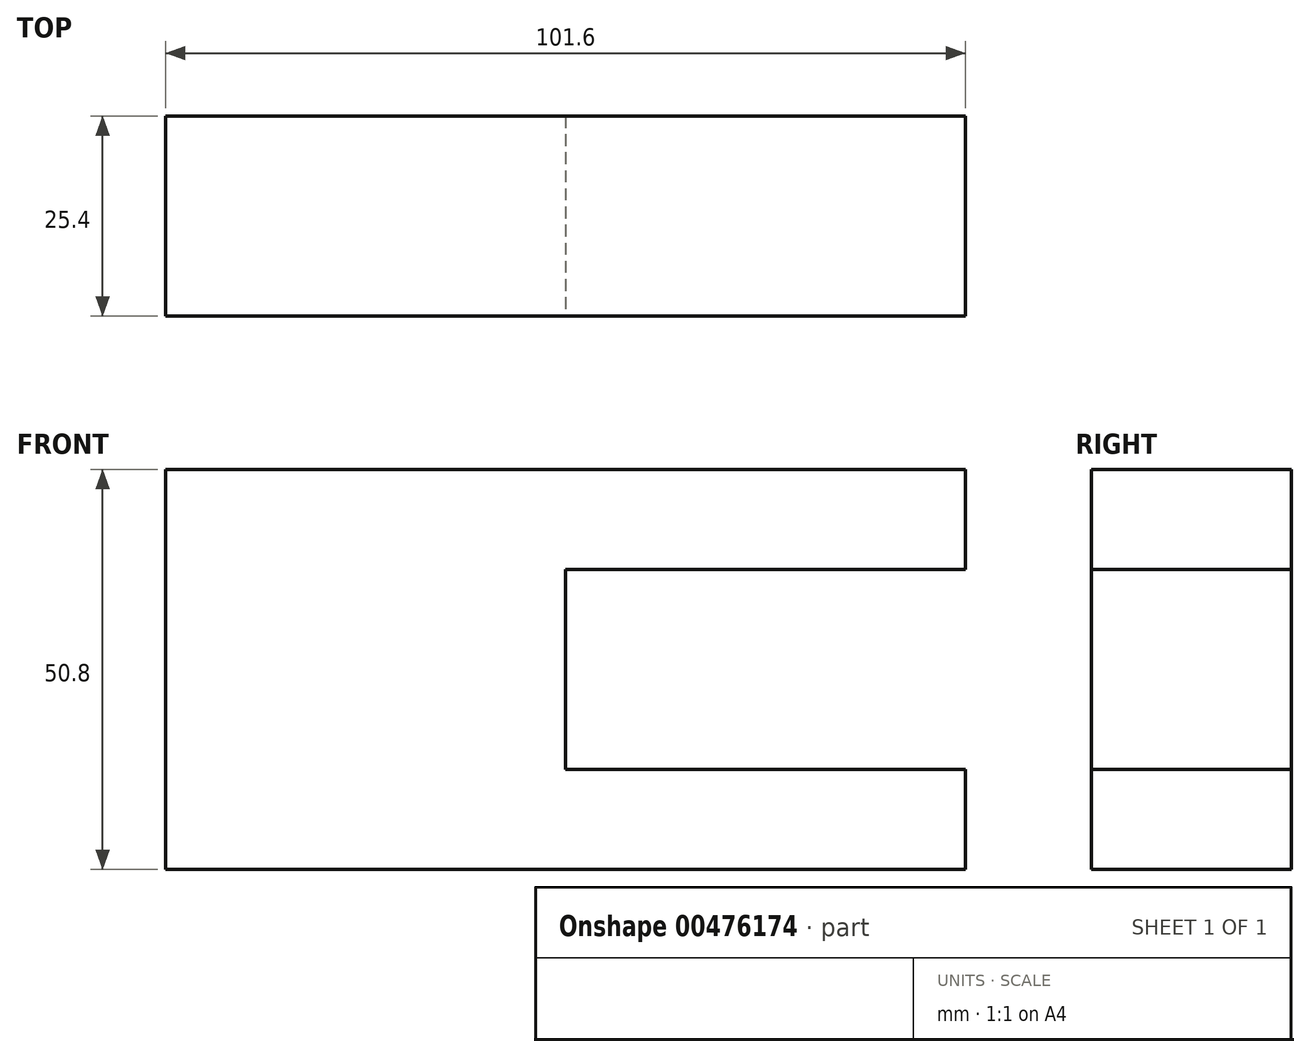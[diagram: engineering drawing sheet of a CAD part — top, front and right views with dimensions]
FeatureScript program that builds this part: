
annotation { "Feature Type Name" : "Feature", "Feature Type Description" : "" }
export const myFeature = defineFeature(function(context is Context, id is Id, definition is map)
    precondition{}
    {
        {
            var Q0;
            Q0=qCreatedBy(makeId("Front.planeOp"),FACE);
            var sketch = newSketch(context, id + "F0", { "sketchPlane" : qUnion([Q0])});
            skLineSegment(sketch, "E0.bottom", {"start": v(50.8, -25.4) * mm, "end": v(-50.8, -25.4) * mm});
            skLineSegment(sketch, "E0.top", {"start": v(50.8, 25.4) * mm, "end": v(-50.8, 25.4) * mm});
            skLineSegment(sketch, "E0.left", {"start": v(50.8, -25.4) * mm, "end": v(50.8, 25.4) * mm});
            skLineSegment(sketch, "E0.right", {"start": v(-50.8, -25.4) * mm, "end": v(-50.8, 25.4) * mm});
            skPoint(sketch, "E0.middle", {"position": v(0, 0) * mm});
            skSolve(sketch);
        }
        {
            var Q0;
            Q0=qSketchRegion(id+"F0",true);
            extrude(context, id + "F1", {"entities" : qUnion([Q0]), "depth" : 25.4 * mm});
        }
        {
            var Q0;
            Q0=makeQuery(id+"F1.opExtrude","CAP_FACE",FACE,{"disambiguationData":[OSD([sQuery(id+"F0.wireOp",EDGE,"E0.bottom"),sQuery(id+"F0.wireOp",EDGE,"E0.top"),sQuery(id+"F0.wireOp",EDGE,"E0.left"),sQuery(id+"F0.wireOp",EDGE,"E0.right")])],"isStart":false});
            var sketch = newSketch(context, id + "F2", { "sketchPlane" : qUnion([Q0])});
            skLineSegment(sketch, "E1.bottom", {"start": v(50.8, 25.4) * mm, "end": v(42.41, 25.4) * mm});
            skLineSegment(sketch, "E1.top", {"start": v(50.8, 25.4) * mm, "end": v(42.41, 25.4) * mm});
            skLineSegment(sketch, "E1.left", {"start": v(50.8, 25.4) * mm, "end": v(50.8, 25.4) * mm});
            skLineSegment(sketch, "E1.right", {"start": v(42.41, 25.4) * mm, "end": v(42.41, 25.4) * mm});
            skLineSegment(sketch, "E2.bottom", {"start": v(50.8, 12.7) * mm, "end": v(0, 12.7) * mm});
            skLineSegment(sketch, "E2.top", {"start": v(50.8, -12.7) * mm, "end": v(0, -12.7) * mm});
            skLineSegment(sketch, "E2.left", {"start": v(50.8, 12.7) * mm, "end": v(50.8, -12.7) * mm});
            skLineSegment(sketch, "E2.right", {"start": v(0, 12.7) * mm, "end": v(0, -12.7) * mm});
            skSolve(sketch);
        }
        {
            var Q0;
            Q0=qSketchRegion(id+"F2",true);
            extrude(context, id + "F3", {"entities" : qUnion([Q0]), "operationType" : NewBodyOperationType.REMOVE, "oppositeDirection" : true, "depth" : 25.4 * mm});
        }
    });
